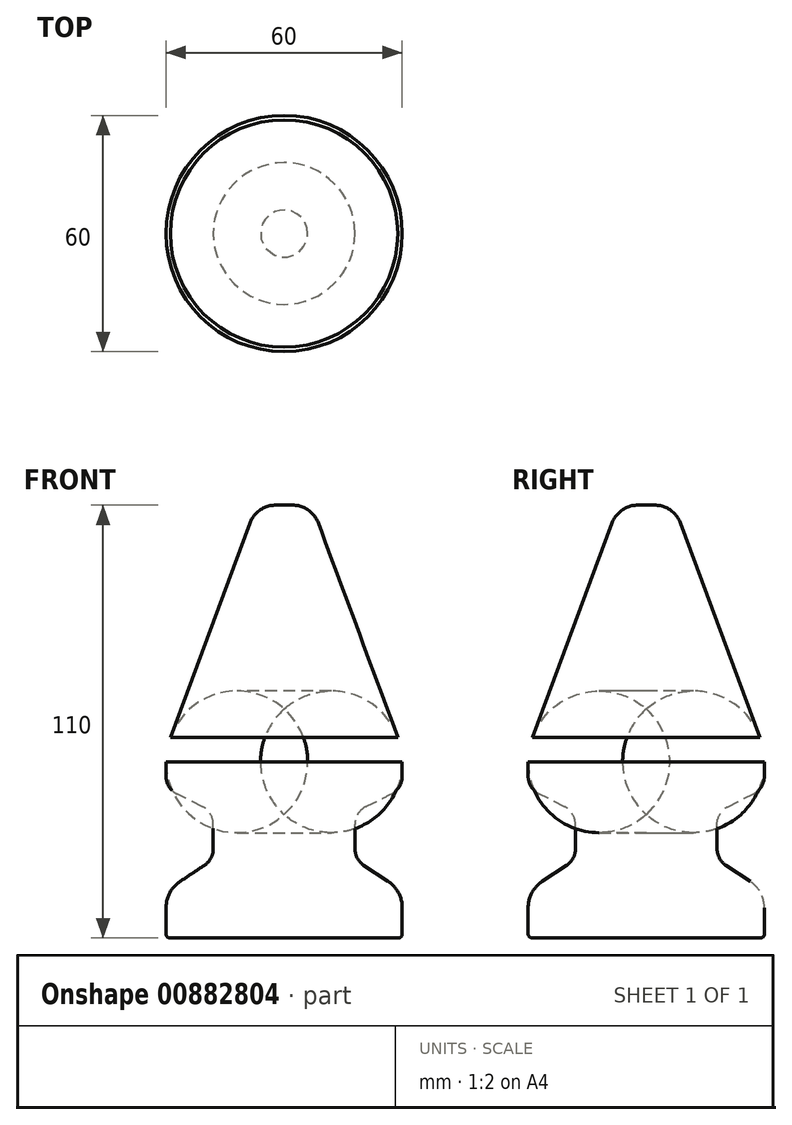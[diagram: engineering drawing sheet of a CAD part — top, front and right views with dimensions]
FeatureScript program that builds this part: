
annotation { "Feature Type Name" : "Feature", "Feature Type Description" : "" }
export const myFeature = defineFeature(function(context is Context, id is Id, definition is map)
    precondition{}
    {
        {
            var Q0;
            Q0=qCreatedBy(makeId("Front.planeOp"),FACE);
            var sketch = newSketch(context, id + "F0", { "sketchPlane" : qUnion([Q0])});
            skLineSegment(sketch, "E0", {"start": v(0, 0) * mm, "end": v(30, 0) * mm});
            skLineSegment(sketch, "E1", {"start": v(30, 0) * mm, "end": v(30, 12) * mm});
            skLineSegment(sketch, "E2", {"start": v(30, 12) * mm, "end": v(18, 20) * mm});
            skLineSegment(sketch, "E3", {"start": v(18, 20) * mm, "end": v(18, 32) * mm});
            skLineSegment(sketch, "E4", {"start": v(18, 32) * mm, "end": v(30, 38) * mm});
            skLineSegment(sketch, "E5", {"start": v(30, 38) * mm, "end": v(30, 48) * mm});
            skLineSegment(sketch, "E6", {"start": v(30, 48) * mm, "end": v(8.7, 105.43) * mm});
            skLineSegment(sketch, "E7", {"start": v(2.13, 110) * mm, "end": v(0, 110) * mm});
            skLineSegment(sketch, "E8", {"start": v(0, 110) * mm, "end": v(0, 0) * mm});
            skPoint(sketch, "E9.visualSharp", {"position": v(7, 110) * mm});
            skArc(sketch, "E9.filletArc", {"start": v(8.7, 105.43) * mm, "mid": v(6.13, 108.75) * mm, "end": v(2.13, 110) * mm});
            skSolve(sketch);
        }
        {
            var Q0;
            Q0 = qSketchRegion(id + "F0", true);
            var Q1;
            Q1=sQuery(id+"F0.wireOp",EDGE,"E8");
            revolve(context, id + "F1", {"surfaceOperationType" : NewSurfaceOperationType.NEW, "entities" : qUnion([Q0]), "axis" : qUnion([Q1]), "revolveType" : RevolveType.FULL});
        }
        {
            var Q0;
            Q0=makeQuery(id+"F1.opRevolve","SWEPT_EDGE",EDGE,{"disambiguationData":[OSD([sQuery(id+"F0.wireOp",EDGE,"E1"),sQuery(id+"F0.wireOp",EDGE,"E2")])]});
            fillet(context, id + "F2", {"entities" : qUnion([Q0]), "radius" : 8 * mm, "tangentPropagation" : true, "allowEdgeOverflow" : false});
        }
        {
            var Q0;
            Q0=makeQuery(id+"F1.opRevolve","SWEPT_EDGE",EDGE,{"disambiguationData":[OSD([sQuery(id+"F0.wireOp",EDGE,"E2"),sQuery(id+"F0.wireOp",EDGE,"E3")])]});
            fillet(context, id + "F3", {"entities" : qUnion([Q0]), "radius" : 5 * mm, "tangentPropagation" : true, "allowEdgeOverflow" : false});
        }
        {
            var Q0;
            Q0=makeQuery(id+"F1.opRevolve","SWEPT_EDGE",EDGE,{"disambiguationData":[OSD([sQuery(id+"F0.wireOp",EDGE,"E3"),sQuery(id+"F0.wireOp",EDGE,"E4")])]});
            fillet(context, id + "F4", {"entities" : qUnion([Q0]), "radius" : 5 * mm, "tangentPropagation" : true, "allowEdgeOverflow" : false});
        }
        {
            var Q0;
            Q0=makeQuery(id+"F1.opRevolve","SWEPT_EDGE",EDGE,{"disambiguationData":[OSD([sQuery(id+"F0.wireOp",EDGE,"E4"),sQuery(id+"F0.wireOp",EDGE,"E5")])]});
            fillet(context, id + "F5", {"entities" : qUnion([Q0]), "radius" : 5 * mm, "tangentPropagation" : true, "allowEdgeOverflow" : false});
        }
        {
            var Q0;
            Q0=makeQuery(id+"F1.opRevolve","SWEPT_EDGE",EDGE,{"disambiguationData":[OSD([sQuery(id+"F0.wireOp",EDGE,"E5"),sQuery(id+"F0.wireOp",EDGE,"E6")])]});
            fillet(context, id + "F6", {"entities" : qUnion([Q0]), "radius" : 18 * mm, "tangentPropagation" : true, "allowEdgeOverflow" : false});
        }
        {
            var Q0;
            Q0=makeQuery(id+"F1.opRevolve","SWEPT_EDGE",EDGE,{"disambiguationData":[OSD([sQuery(id+"F0.wireOp",EDGE,"E0"),sQuery(id+"F0.wireOp",EDGE,"E1")])]});
            fillet(context, id + "F7", {"entities" : qUnion([Q0]), "radius" : 1 * mm, "tangentPropagation" : true, "allowEdgeOverflow" : false});
        }
    });
